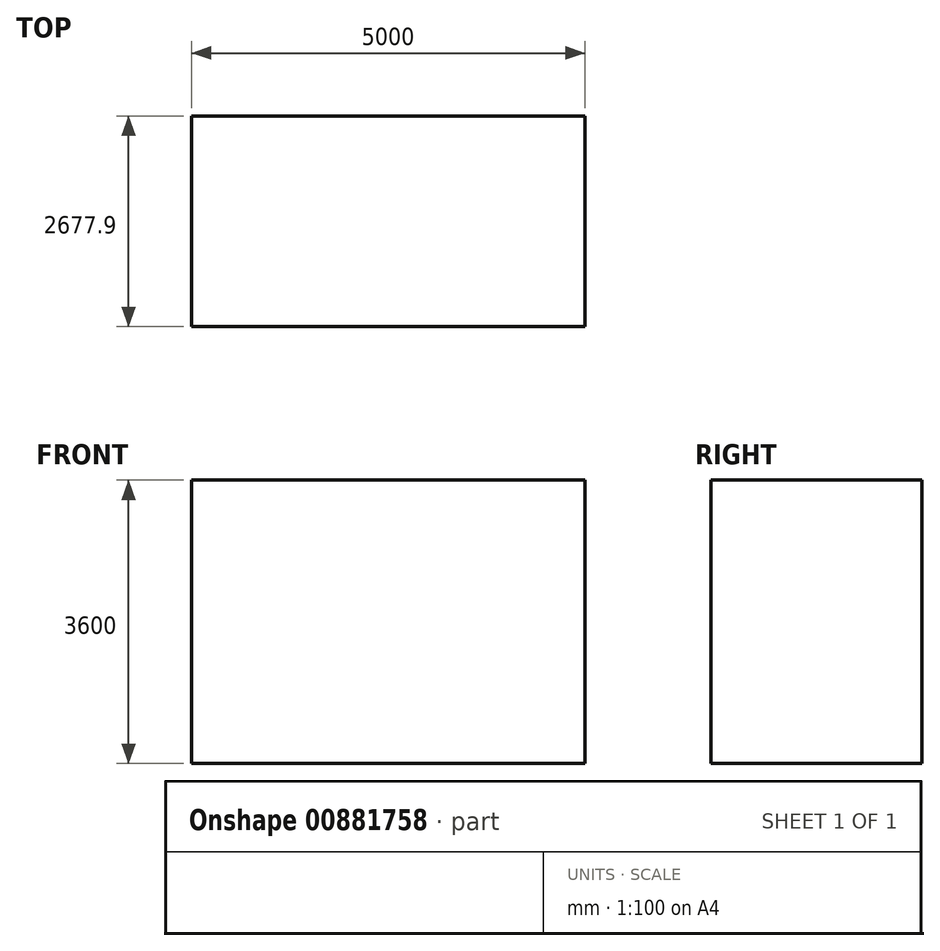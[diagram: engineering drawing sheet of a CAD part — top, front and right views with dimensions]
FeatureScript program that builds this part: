
annotation { "Feature Type Name" : "Feature", "Feature Type Description" : "" }
export const myFeature = defineFeature(function(context is Context, id is Id, definition is map)
    precondition{}
    {
        {
            var Q0;
            Q0=qCreatedBy(makeId("Front.planeOp"),FACE);
            var sketch = newSketch(context, id + "F0", { "sketchPlane" : qUnion([Q0])});
            skLineSegment(sketch, "E0", {"start": v(-1612.45, 1825.33) * mm, "end": v(-1612.45, -1774.67) * mm});
            skLineSegment(sketch, "E1", {"start": v(-1612.45, -1774.67) * mm, "end": v(3387.55, -1774.67) * mm});
            skLineSegment(sketch, "E2", {"start": v(3387.55, -1774.67) * mm, "end": v(3387.55, 1825.33) * mm});
            skLineSegment(sketch, "E3", {"start": v(3387.55, 1825.33) * mm, "end": v(-1612.45, 1825.33) * mm});
            skLineSegment(sketch, "E4", {"start": v(-219.08, -875.9) * mm, "end": v(3005.64, 1344.53) * mm});
            skSolve(sketch);
        }
        {
            var Q0;
            Q0=makeQuery(id+"F0.imprint","IMPRINT",FACE,{"disambiguationData":[TD([[makeQuery(id+"F0.imprint","IMPRINT",EDGE,{"derivedFrom":sQuery(id+"F0.wireOp",EDGE,"E0")}),1.0]])]});
            var sketch = newSketch(context, id + "F1", { "sketchPlane" : qUnion([Q0])});
            skSolve(sketch);
        }
        {
            var Q0;
            Q0=makeQuery(id+"F1.imprint","IMPRINT",FACE,{"disambiguationData":[TD([[makeQuery(id+"F1.imprint","IMPRINT",EDGE,{"derivedFrom":makeQuery(id+"F0.imprint","IMPRINT",EDGE,{"derivedFrom":sQuery(id+"F0.wireOp",EDGE,"E0")})}),1.0]])]});
            extrude(context, id + "F2", {"entities" : qUnion([Q0]), "depth" : 2677.9 * mm, "offsetDistance" : 25 * mm});
        }
        {
            var Q0;
            Q0=sQuery(id+"F0.wireOp",EDGE,"E4");
            extrude(context, id + "F3", {"bodyType" : ToolBodyType.SURFACE, "surfaceEntities" : qUnion([Q0]), "depth" : 3099.97 * mm, "offsetDistance" : 25 * mm});
        }
    });
